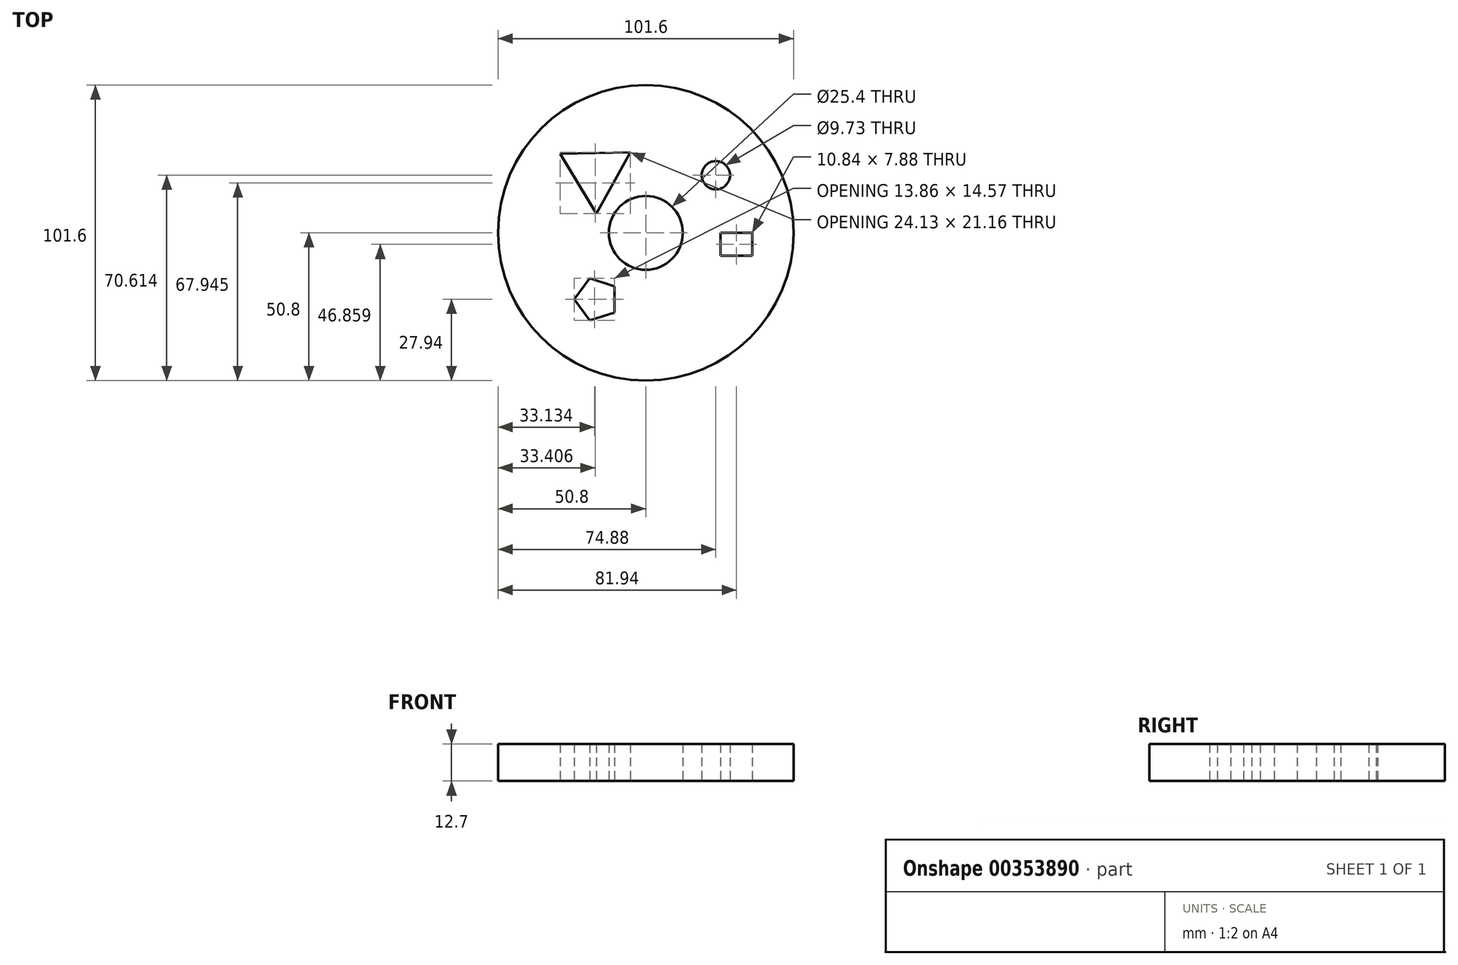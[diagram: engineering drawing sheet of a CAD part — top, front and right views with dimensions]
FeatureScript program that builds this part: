
annotation { "Feature Type Name" : "Feature", "Feature Type Description" : "" }
export const myFeature = defineFeature(function(context is Context, id is Id, definition is map)
    precondition{}
    {
        {
            var Q0;
            Q0=qCreatedBy(makeId("Top.planeOp"),FACE);
            var sketch = newSketch(context, id + "F0", { "sketchPlane" : qUnion([Q0])});
            skCircle(sketch, "E0", {"center": v(0, 0) * mm, "radius": 50.8 * mm});
            skCircle(sketch, "E1", {"center": v(0, 0) * mm, "radius": 12.7 * mm});
            skCircle(sketch, "E2.cCircle", {"center": v(-17.24, 20.5) * mm, "radius": 6.97 * mm, "construction": true});
            skLineSegment(sketch, "E2.0", {"start": v(-5.33, 27.73) * mm, "end": v(-16.93, 6.56) * mm});
            skLineSegment(sketch, "E2.1", {"start": v(-16.93, 6.56) * mm, "end": v(-29.46, 27.2) * mm});
            skLineSegment(sketch, "E2.2", {"start": v(-29.46, 27.2) * mm, "end": v(-5.33, 27.73) * mm});
            skPoint(sketch, "E2.0.midPoint", {"position": v(-11.13, 17.15) * mm});
            skCircle(sketch, "E3.cCircle", {"center": v(-16.93, -22.86) * mm, "radius": 6.2 * mm, "construction": true});
            skLineSegment(sketch, "E3.0", {"start": v(-10.74, -18.36) * mm, "end": v(-10.74, -27.36) * mm});
            skLineSegment(sketch, "E3.1", {"start": v(-10.74, -27.36) * mm, "end": v(-19.3, -30.14) * mm});
            skLineSegment(sketch, "E3.2", {"start": v(-19.3, -30.14) * mm, "end": v(-24.6, -22.86) * mm});
            skLineSegment(sketch, "E3.3", {"start": v(-24.6, -22.86) * mm, "end": v(-19.3, -15.58) * mm});
            skLineSegment(sketch, "E3.4", {"start": v(-19.3, -15.58) * mm, "end": v(-10.74, -18.36) * mm});
            skPoint(sketch, "E3.0.midPoint", {"position": v(-10.74, -22.86) * mm});
            skLineSegment(sketch, "E4.bottom", {"start": v(36.56, 0) * mm, "end": v(25.72, 0) * mm});
            skLineSegment(sketch, "E4.top", {"start": v(36.56, -7.88) * mm, "end": v(25.72, -7.88) * mm});
            skLineSegment(sketch, "E4.left", {"start": v(36.56, 0) * mm, "end": v(36.56, -7.88) * mm});
            skLineSegment(sketch, "E4.right", {"start": v(25.72, 0) * mm, "end": v(25.72, -7.88) * mm});
            skCircle(sketch, "E5", {"center": v(24.08, 19.81) * mm, "radius": 4.87 * mm});
            skSolve(sketch);
        }
        {
            var Q0;
            Q0 = qSketchRegion(id + "F0", true);
            extrude(context, id + "F1", {"entities" : qUnion([Q0]), "endBound" : BoundingType.SYMMETRIC, "depth" : 12.7 * mm});
        }
    });
